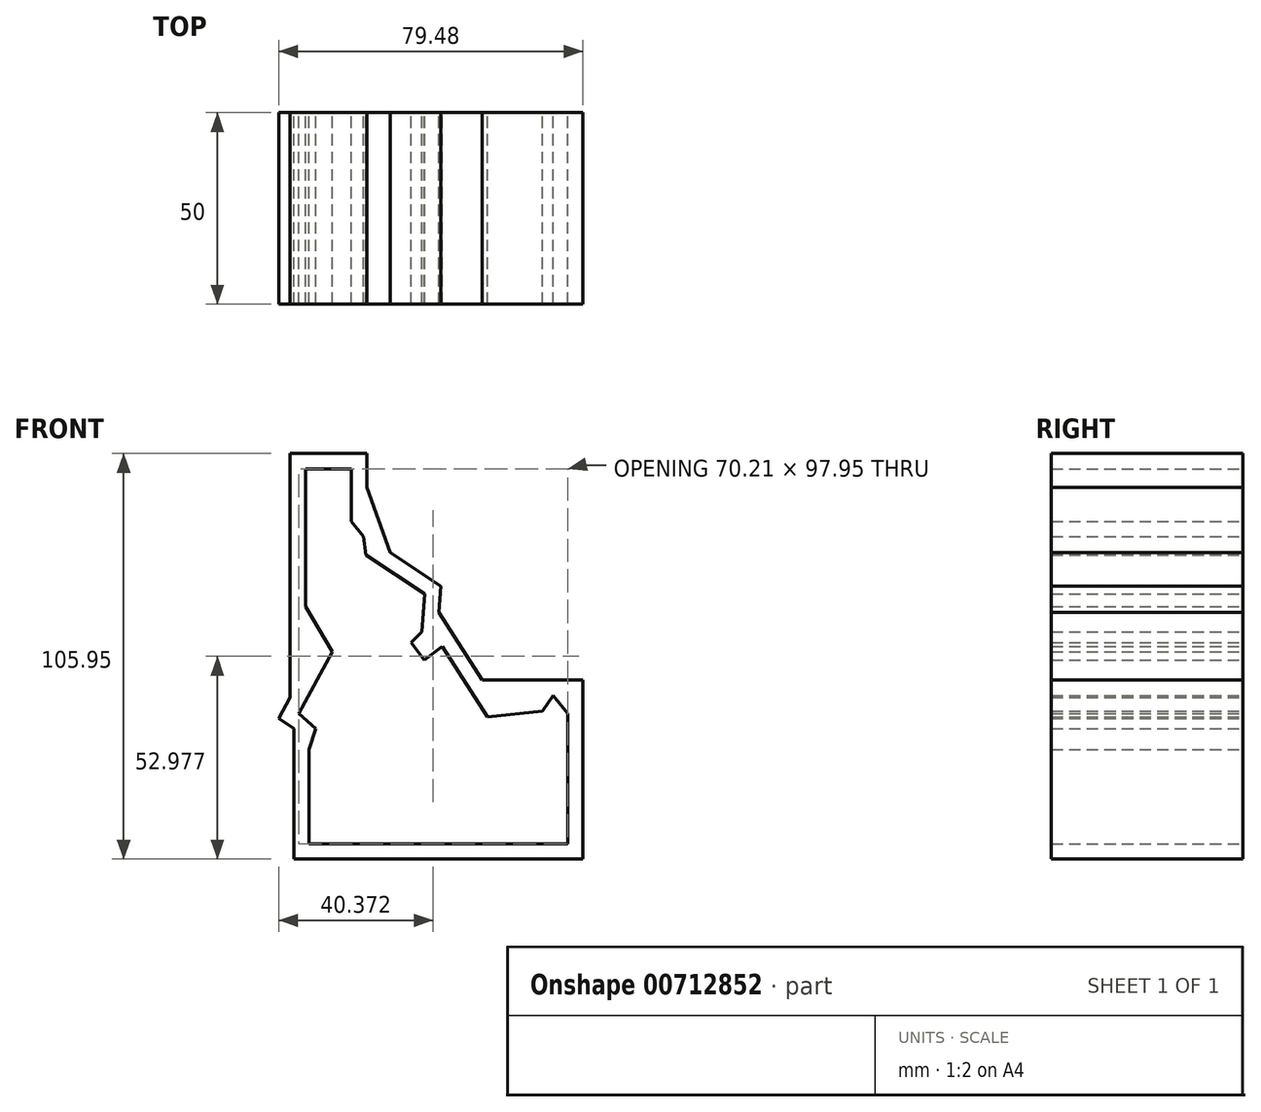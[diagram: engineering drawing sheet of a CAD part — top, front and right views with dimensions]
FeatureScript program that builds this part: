
annotation { "Feature Type Name" : "Feature", "Feature Type Description" : "" }
export const myFeature = defineFeature(function(context is Context, id is Id, definition is map)
    precondition{}
    {
        {
            var Q0;
            Q0=qCreatedBy(makeId("Front.planeOp"),FACE);
            var sketch = newSketch(context, id + "F0", { "sketchPlane" : qUnion([Q0])});
            skLineSegment(sketch, "E0", {"start": v(-70.38, 63.32) * mm, "end": v(-70.38, 99.33) * mm});
            skLineSegment(sketch, "E1", {"start": v(-70.38, 99.33) * mm, "end": v(-58.38, 99.33) * mm});
            skLineSegment(sketch, "E2", {"start": v(-58.38, 99.33) * mm, "end": v(-58.38, 85.53) * mm});
            skLineSegment(sketch, "E3", {"start": v(-58.38, 85.53) * mm, "end": v(-55.21, 81.6) * mm});
            skLineSegment(sketch, "E4", {"start": v(-55.21, 81.6) * mm, "end": v(-54.56, 76.85) * mm});
            skLineSegment(sketch, "E5", {"start": v(-54.56, 76.85) * mm, "end": v(-39.18, 66.7) * mm});
            skLineSegment(sketch, "E6", {"start": v(-39.18, 66.7) * mm, "end": v(-40, 56.72) * mm});
            skLineSegment(sketch, "E7", {"start": v(-40, 56.72) * mm, "end": v(-42.76, 53.94) * mm});
            skLineSegment(sketch, "E8", {"start": v(-42.76, 53.94) * mm, "end": v(-39.32, 49.36) * mm});
            skLineSegment(sketch, "E9", {"start": v(-39.32, 49.36) * mm, "end": v(-34.61, 52.9) * mm});
            skLineSegment(sketch, "E10", {"start": v(-34.61, 52.9) * mm, "end": v(-22.85, 34.58) * mm});
            skLineSegment(sketch, "E11", {"start": v(-22.85, 34.58) * mm, "end": v(-8.45, 36.05) * mm});
            skLineSegment(sketch, "E12", {"start": v(-8.45, 36.05) * mm, "end": v(-5.67, 40.14) * mm});
            skLineSegment(sketch, "E13", {"start": v(-5.67, 40.14) * mm, "end": v(-1.9, 35.4) * mm});
            skLineSegment(sketch, "E14", {"start": v(-1.9, 35.4) * mm, "end": v(-1.9, 1.38) * mm});
            skLineSegment(sketch, "E15", {"start": v(-1.9, 1.38) * mm, "end": v(-69.4, 1.38) * mm});
            skLineSegment(sketch, "E16", {"start": v(-69.4, 1.38) * mm, "end": v(-69.4, 26) * mm});
            skLineSegment(sketch, "E17", {"start": v(-69.4, 26) * mm, "end": v(-67.7, 31.5) * mm});
            skLineSegment(sketch, "E18", {"start": v(-67.7, 31.5) * mm, "end": v(-72.11, 35.4) * mm});
            skLineSegment(sketch, "E19", {"start": v(-72.11, 35.4) * mm, "end": v(-63.3, 51.58) * mm});
            skLineSegment(sketch, "E20", {"start": v(-63.3, 51.58) * mm, "end": v(-70.38, 63.32) * mm});
            skLineSegment(sketch, "E21.0", {"start": v(-54.38, 103.33) * mm, "end": v(-54.38, 94.43) * mm});
            skLineSegment(sketch, "E21.1", {"start": v(-74.38, 103.33) * mm, "end": v(-54.38, 103.33) * mm});
            skLineSegment(sketch, "E21.2", {"start": v(-74.38, 39.6) * mm, "end": v(-74.38, 103.33) * mm});
            skLineSegment(sketch, "E22.0", {"start": v(-77.38, 34.08) * mm, "end": v(-74.38, 39.6) * mm});
            skLineSegment(sketch, "E23.0", {"start": v(-73.4, -2.62) * mm, "end": v(-73.4, 31.46) * mm});
            skLineSegment(sketch, "E23.1", {"start": v(2.1, -2.62) * mm, "end": v(-73.4, -2.62) * mm});
            skLineSegment(sketch, "E23.2", {"start": v(2.1, 44.14) * mm, "end": v(2.1, -2.62) * mm});
            skLineSegment(sketch, "E24.0", {"start": v(-35, 68.74) * mm, "end": v(-35.57, 61.79) * mm});
            skLineSegment(sketch, "E24.1", {"start": v(-48.28, 77.5) * mm, "end": v(-35, 68.74) * mm});
            skLineSegment(sketch, "E25.0", {"start": v(-35.57, 61.79) * mm, "end": v(-24.24, 44.14) * mm});
            skLineSegment(sketch, "E26", {"start": v(-77.38, 34.08) * mm, "end": v(-73.4, 31.46) * mm});
            skLineSegment(sketch, "E27", {"start": v(-54.38, 94.43) * mm, "end": v(-48.28, 77.5) * mm});
            skPoint(sketch, "E28.orphan", {"position": v(-54.38, 85.53) * mm});
            skPoint(sketch, "E29.orphan", {"position": v(-36.14, 54.83) * mm});
            skLineSegment(sketch, "E30", {"start": v(2.1, 44.14) * mm, "end": v(-24.24, 44.14) * mm});
            skSolve(sketch);
        }
        {
            var Q0;
            Q0=qSketchRegion(id+"F0",true);
            extrude(context, id + "F1", {"entities" : qUnion([Q0]), "depth" : 50 * mm, "offsetDistance" : 25 * mm});
        }
    });
